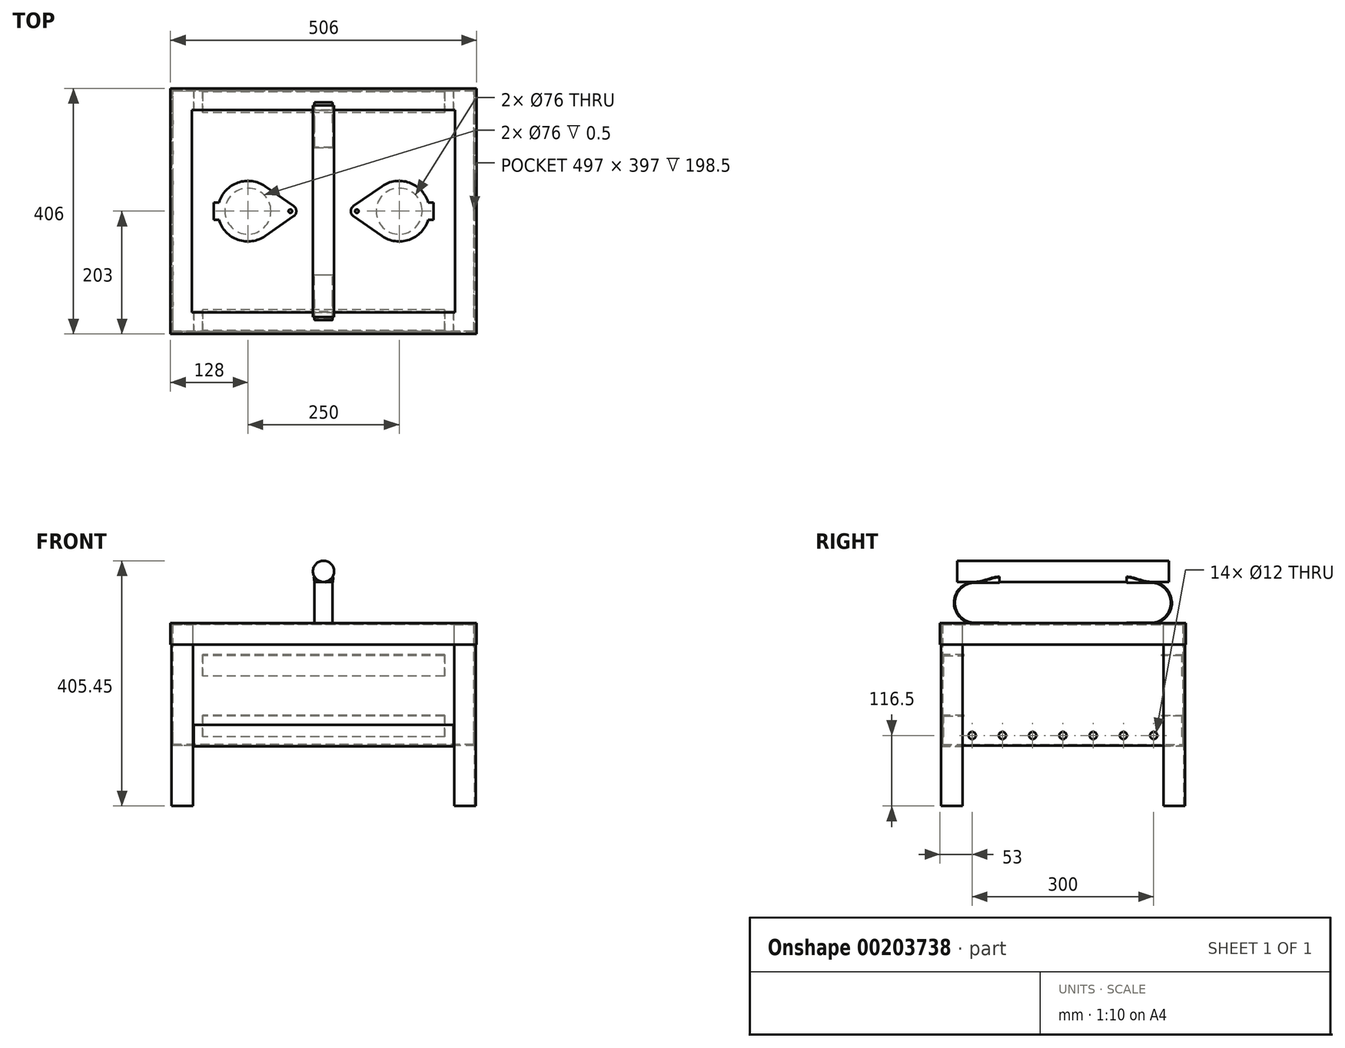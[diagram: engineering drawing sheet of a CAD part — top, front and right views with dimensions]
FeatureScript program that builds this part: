
annotation { "Feature Type Name" : "Feature", "Feature Type Description" : "" }
export const myFeature = defineFeature(function(context is Context, id is Id, definition is map)
    precondition{}
    {
        {
            var Q0;
            Q0=qCreatedBy(makeId("Top.planeOp"),FACE);
            var sketch = newSketch(context, id + "F0", { "sketchPlane" : qUnion([Q0])});
            skLineSegment(sketch, "E0.bottom", {"start": v(250, -200) * mm, "end": v(-250, -200) * mm});
            skLineSegment(sketch, "E0.top", {"start": v(250, 200) * mm, "end": v(-250, 200) * mm});
            skLineSegment(sketch, "E0.left", {"start": v(250, -200) * mm, "end": v(250, 200) * mm});
            skLineSegment(sketch, "E0.right", {"start": v(-250, -200) * mm, "end": v(-250, 200) * mm});
            skPoint(sketch, "E0.middle", {"position": v(0, 0) * mm});
            skSolve(sketch);
        }
        {
            var Q0;
            Q0 = qSketchRegion(id + "F0", true);
            extrude(context, id + "F1", {"entities" : qUnion([Q0]), "oppositeDirection" : true, "depth" : 200 * mm});
        }
        {
            var Q0;
            Q0=makeQuery(id+"F1.opExtrude","CAP_FACE",FACE,{"disambiguationData":[OSD([sQuery(id+"F0.wireOp",EDGE,"E0.bottom"),sQuery(id+"F0.wireOp",EDGE,"E0.top"),sQuery(id+"F0.wireOp",EDGE,"E0.left"),sQuery(id+"F0.wireOp",EDGE,"E0.right")])],"isStart":true});
            shell(context, id + "F2", {"entities" : qUnion([Q0]), "thickness" : 1.5 * mm});
        }
        {
            var Q0;
            Q0=qCreatedBy(makeId("Top.planeOp"),FACE);
            var sketch = newSketch(context, id + "F3", { "sketchPlane" : qUnion([Q0])});
            skLineSegment(sketch, "E1", {"start": v(-216, 201.5) * mm, "end": v(-251.5, 201.5) * mm});
            skLineSegment(sketch, "E2", {"start": v(-251.5, 201.5) * mm, "end": v(-251.5, 166) * mm});
            skLineSegment(sketch, "E3", {"start": v(-251.5, 166) * mm, "end": v(-250, 166) * mm});
            skLineSegment(sketch, "E4", {"start": v(-250, 166) * mm, "end": v(-250, 200) * mm});
            skLineSegment(sketch, "E5", {"start": v(-250, 200) * mm, "end": v(-216, 200) * mm});
            skLineSegment(sketch, "E6", {"start": v(-216, 200) * mm, "end": v(-216, 201.5) * mm});
            skSolve(sketch);
        }
        {
            var Q0;
            Q0 = qSketchRegion(id + "F3", true);
            var Q1;
            Q1=makeQuery(id+"F1.opExtrude","CAP_FACE",FACE,{"disambiguationData":[OSD([sQuery(id+"F0.wireOp",EDGE,"E0.bottom"),sQuery(id+"F0.wireOp",EDGE,"E0.top"),sQuery(id+"F0.wireOp",EDGE,"E0.left"),sQuery(id+"F0.wireOp",EDGE,"E0.right")])],"isStart":false});
            extrude(context, id + "F4", {"entities" : qUnion([Q0]), "oppositeDirection" : true, "endBoundEntityFace" : qUnion([Q1]), "depth" : 300 * mm});
        }
        {
            var Q0;
            Q0=makeQuery(id+"F4.opExtrude","SWEPT_BODY",BODY,{"disambiguationData":[OSD([sQuery(id+"F3.wireOp",EDGE,"E1"),sQuery(id+"F3.wireOp",EDGE,"E2"),sQuery(id+"F3.wireOp",EDGE,"E3"),sQuery(id+"F3.wireOp",EDGE,"E4"),sQuery(id+"F3.wireOp",EDGE,"E5"),sQuery(id+"F3.wireOp",EDGE,"E6")])]});
            var Q1;
            Q1=qCreatedBy(makeId("Front.planeOp"),FACE);
            mirror(context, id + "F5", {"entities" : qUnion([Q0]), "mirrorPlane" : qUnion([Q1])});
        }
        {
            var Q0;
            Q0=makeQuery(id+"F4.opExtrude","SWEPT_BODY",BODY,{"disambiguationData":[OSD([sQuery(id+"F3.wireOp",EDGE,"E1"),sQuery(id+"F3.wireOp",EDGE,"E2"),sQuery(id+"F3.wireOp",EDGE,"E3"),sQuery(id+"F3.wireOp",EDGE,"E4"),sQuery(id+"F3.wireOp",EDGE,"E5"),sQuery(id+"F3.wireOp",EDGE,"E6")])]});
            var Q1;
            Q1=makeQuery(id+"F5.opPattern","COPY",BODY,{"derivedFrom":makeQuery(id+"F4.opExtrude","SWEPT_BODY",BODY,{"disambiguationData":[OSD([sQuery(id+"F3.wireOp",EDGE,"E1"),sQuery(id+"F3.wireOp",EDGE,"E2"),sQuery(id+"F3.wireOp",EDGE,"E3"),sQuery(id+"F3.wireOp",EDGE,"E4"),sQuery(id+"F3.wireOp",EDGE,"E5"),sQuery(id+"F3.wireOp",EDGE,"E6")])]}),"instanceName":"1"});
            var Q2;
            Q2=qCreatedBy(makeId("Right.planeOp"),FACE);
            mirror(context, id + "F6", {"entities" : qUnion([Q0, Q1]), "mirrorPlane" : qUnion([Q2])});
        }
        {
            var Q0;
            Q0=qCreatedBy(makeId("Right.planeOp"),FACE);
            var sketch = newSketch(context, id + "F7", { "sketchPlane" : qUnion([Q0])});
            skLineSegment(sketch, "E7", {"start": v(163, -150) * mm, "end": v(198.5, -150) * mm});
            skLineSegment(sketch, "E8", {"start": v(198.5, -150) * mm, "end": v(198.5, -185.5) * mm});
            skLineSegment(sketch, "E9", {"start": v(198.5, -185.5) * mm, "end": v(197, -185.5) * mm});
            skLineSegment(sketch, "E10", {"start": v(197, -185.5) * mm, "end": v(197, -151.5) * mm});
            skLineSegment(sketch, "E11", {"start": v(197, -151.5) * mm, "end": v(163, -151.5) * mm});
            skLineSegment(sketch, "E12", {"start": v(163, -151.5) * mm, "end": v(163, -150) * mm});
            skSolve(sketch);
        }
        {
            var Q0;
            Q0 = qSketchRegion(id + "F7", true);
            extrude(context, id + "F8", {"entities" : qUnion([Q0]), "endBound" : BoundingType.SYMMETRIC, "depth" : 400 * mm});
        }
        {
            var Q0;
            Q0=makeQuery(id+"F8.opExtrude","SWEPT_BODY",BODY,{"disambiguationData":[OSD([sQuery(id+"F7.wireOp",EDGE,"E7"),sQuery(id+"F7.wireOp",EDGE,"E8"),sQuery(id+"F7.wireOp",EDGE,"E9"),sQuery(id+"F7.wireOp",EDGE,"E10"),sQuery(id+"F7.wireOp",EDGE,"E11"),sQuery(id+"F7.wireOp",EDGE,"E12")])]});
            var Q1;
            Q1=qCreatedBy(makeId("Front.planeOp"),FACE);
            mirror(context, id + "F9", {"entities" : qUnion([Q0]), "mirrorPlane" : qUnion([Q1])});
        }
        {
            var Q0;
            Q0=makeQuery(id+"F8.opExtrude","SWEPT_BODY",BODY,{"disambiguationData":[OSD([sQuery(id+"F7.wireOp",EDGE,"E7"),sQuery(id+"F7.wireOp",EDGE,"E8"),sQuery(id+"F7.wireOp",EDGE,"E9"),sQuery(id+"F7.wireOp",EDGE,"E10"),sQuery(id+"F7.wireOp",EDGE,"E11"),sQuery(id+"F7.wireOp",EDGE,"E12")])]});
            var Q1;
            Q1=makeQuery(id+"F9.opPattern","COPY",BODY,{"derivedFrom":makeQuery(id+"F8.opExtrude","SWEPT_BODY",BODY,{"disambiguationData":[OSD([sQuery(id+"F7.wireOp",EDGE,"E7"),sQuery(id+"F7.wireOp",EDGE,"E8"),sQuery(id+"F7.wireOp",EDGE,"E9"),sQuery(id+"F7.wireOp",EDGE,"E10"),sQuery(id+"F7.wireOp",EDGE,"E11"),sQuery(id+"F7.wireOp",EDGE,"E12")])]}),"instanceName":"1"});
            var Q2;
            Q2=makeQuery(id+"F1.opExtrude","SWEPT_EDGE",EDGE,{"disambiguationData":[OSD([sQuery(id+"F0.wireOp",EDGE,"E0.top"),sQuery(id+"F0.wireOp",EDGE,"E0.right")])]});
            transform(context, id + "F10", {"entities" : qUnion([Q0, Q1]), "transformType" : TransformType.TRANSLATION_DISTANCE, "transformDirection" : qUnion([Q2]), "distance" : 100 * mm, "makeCopy" : true});
        }
        {
            var Q0;
            Q0=makeQuery(id+"F1.opExtrude","SWEPT_FACE",FACE,{"disambiguationData":[OSD([sQuery(id+"F0.wireOp",EDGE,"E0.right")])]});
            var sketch = newSketch(context, id + "F11", { "sketchPlane" : qUnion([Q0])});
            skLineSegment(sketch, "E13", {"start": v(-221.22, -183.5) * mm, "end": v(207.24, -183.5) * mm, "construction": true});
            skCircle(sketch, "E14", {"center": v(0, -183.5) * mm, "radius": 6 * mm});
            skPoint(sketch, "E14.centerSnap0", {"position": v(-7, -183.5) * mm});
            skCircle(sketch, "E15.1.0.0", {"center": v(50, -183.5) * mm, "radius": 6 * mm});
            skCircle(sketch, "E15.2.0.0", {"center": v(100, -183.5) * mm, "radius": 6 * mm});
            skCircle(sketch, "E15.3.0.0", {"center": v(150, -183.5) * mm, "radius": 6 * mm});
            skLineSegment(sketch, "E15.direction1", {"start": v(0, -183.5) * mm, "end": v(50, -183.5) * mm, "construction": true});
            skCircle(sketch, "E16.1.0.0", {"center": v(-50, -183.5) * mm, "radius": 6 * mm});
            skCircle(sketch, "E16.2.0.0", {"center": v(-100, -183.5) * mm, "radius": 6 * mm});
            skCircle(sketch, "E16.3.0.0", {"center": v(-150, -183.5) * mm, "radius": 6 * mm});
            skLineSegment(sketch, "E16.direction1", {"start": v(0, -183.5) * mm, "end": v(-50, -183.5) * mm, "construction": true});
            skSolve(sketch);
        }
        {
            var Q0;
            Q0 = qSketchRegion(id + "F11", true);
            extrude(context, id + "F12", {"entities" : qUnion([Q0]), "operationType" : NewBodyOperationType.REMOVE, "endBound" : BoundingType.THROUGH_ALL, "oppositeDirection" : true, "depth" : 25 * mm});
        }
        {
            var Q0;
            Q0=qCreatedBy(makeId("Top.planeOp"),FACE);
            var sketch = newSketch(context, id + "F13", { "sketchPlane" : qUnion([Q0])});
            skLineSegment(sketch, "E17.bottom", {"start": v(-250, 200) * mm, "end": v(250, 200) * mm});
            skLineSegment(sketch, "E17.top", {"start": v(-250, -200) * mm, "end": v(250, -200) * mm});
            skLineSegment(sketch, "E17.left", {"start": v(-250, 200) * mm, "end": v(-250, -200) * mm});
            skLineSegment(sketch, "E17.right", {"start": v(250, 200) * mm, "end": v(250, -200) * mm});
            skSolve(sketch);
        }
        {
            var Q0;
            Q0 = qSketchRegion(id + "F13", true);
            extrude(context, id + "F14", {"entities" : qUnion([Q0]), "depth" : 1.5 * mm});
        }
        {
            var Q0;
            Q0=makeQuery(id+"F14.opExtrude","CAP_FACE",FACE,{"disambiguationData":[OSD([sQuery(id+"F13.wireOp",EDGE,"E17.bottom"),sQuery(id+"F13.wireOp",EDGE,"E17.top"),sQuery(id+"F13.wireOp",EDGE,"E17.left"),sQuery(id+"F13.wireOp",EDGE,"E17.right")])],"isStart":false});
            cPlane(context, id + "F15", {"entities" : qUnion([Q0]), "cplaneType" : CPlaneType.OFFSET, "offset" : 1 * mm, "width" : 150 * mm, "height" : 150 * mm});
        }
        {
            var Q0;
            Q0=qCreatedBy(id+"F15.planeOp",FACE);
            var sketch = newSketch(context, id + "F16", { "sketchPlane" : qUnion([Q0])});
            skLineSegment(sketch, "E18.0", {"start": v(-251.5, 201.5) * mm, "end": v(-251.5, 166) * mm, "construction": true});
            skLineSegment(sketch, "E19.0", {"start": v(-216, 201.5) * mm, "end": v(-251.5, 201.5) * mm, "construction": true});
            skLineSegment(sketch, "E20.bottom", {"start": v(-253, 203) * mm, "end": v(253, 203) * mm});
            skLineSegment(sketch, "E20.top", {"start": v(-253, -203) * mm, "end": v(253, -203) * mm});
            skLineSegment(sketch, "E20.left", {"start": v(-253, 203) * mm, "end": v(-253, -203) * mm});
            skLineSegment(sketch, "E20.right", {"start": v(253, 203) * mm, "end": v(253, -203) * mm});
            skLineSegment(sketch, "E21.0", {"start": v(216, -201.5) * mm, "end": v(251.5, -201.5) * mm, "construction": true});
            skLineSegment(sketch, "E22.0", {"start": v(251.5, -201.5) * mm, "end": v(251.5, -166) * mm, "construction": true});
            skSolve(sketch);
        }
        {
            var Q0;
            Q0 = qSketchRegion(id + "F16", true);
            extrude(context, id + "F17", {"entities" : qUnion([Q0]), "oppositeDirection" : true, "depth" : 35.5 * mm});
        }
        {
            var Q0;
            Q0=makeQuery(id+"F17.opExtrude","CAP_FACE",FACE,{"disambiguationData":[OSD([sQuery(id+"F16.wireOp",EDGE,"E20.bottom"),sQuery(id+"F16.wireOp",EDGE,"E20.top"),sQuery(id+"F16.wireOp",EDGE,"E20.left"),sQuery(id+"F16.wireOp",EDGE,"E20.right")])],"isStart":false});
            shell(context, id + "F18", {"entities" : qUnion([Q0]), "thickness" : 1.5 * mm});
        }
        {
            var Q0;
            Q0=makeQuery(id+"F17.opExtrude","CAP_FACE",FACE,{"disambiguationData":[OSD([sQuery(id+"F16.wireOp",EDGE,"E20.bottom"),sQuery(id+"F16.wireOp",EDGE,"E20.top"),sQuery(id+"F16.wireOp",EDGE,"E20.left"),sQuery(id+"F16.wireOp",EDGE,"E20.right")])],"isStart":true});
            var sketch = newSketch(context, id + "F19", { "sketchPlane" : qUnion([Q0])});
            skLineSegment(sketch, "E23.bottom", {"start": v(-217.5, 167.5) * mm, "end": v(217.5, 167.5) * mm});
            skLineSegment(sketch, "E23.top", {"start": v(-217.5, -167.5) * mm, "end": v(217.5, -167.5) * mm});
            skLineSegment(sketch, "E23.left", {"start": v(-217.5, 167.5) * mm, "end": v(-217.5, -167.5) * mm});
            skLineSegment(sketch, "E23.right", {"start": v(217.5, 167.5) * mm, "end": v(217.5, -167.5) * mm});
            skSolve(sketch);
        }
        {
            var Q0;
            Q0 = qSketchRegion(id + "F19", true);
            extrude(context, id + "F20", {"entities" : qUnion([Q0]), "operationType" : NewBodyOperationType.REMOVE, "endBound" : BoundingType.UP_TO_NEXT, "oppositeDirection" : true, "depth" : 25 * mm});
        }
        {
            var Q0;
            Q0=makeQuery(id+"F14.opExtrude","CAP_FACE",FACE,{"disambiguationData":[OSD([sQuery(id+"F13.wireOp",EDGE,"E17.bottom"),sQuery(id+"F13.wireOp",EDGE,"E17.top"),sQuery(id+"F13.wireOp",EDGE,"E17.left"),sQuery(id+"F13.wireOp",EDGE,"E17.right")])],"isStart":false});
            var sketch = newSketch(context, id + "F21", { "sketchPlane" : qUnion([Q0])});
            skLineSegment(sketch, "E24", {"start": v(-340.59, 0) * mm, "end": v(391.54, 0) * mm, "construction": true});
            skPoint(sketch, "E24.startSnap0", {"position": v(-250, 0) * mm});
            skPoint(sketch, "E24.endSnap0", {"position": v(-250, 0) * mm});
            skLineSegment(sketch, "E25", {"start": v(0, 278) * mm, "end": v(0, -285.77) * mm, "construction": true});
            skCircle(sketch, "E26", {"center": v(-125, 0) * mm, "radius": 38 * mm});
            skCircle(sketch, "E27", {"center": v(125, 0) * mm, "radius": 38 * mm});
            skSolve(sketch);
        }
        {
            var Q0;
            Q0 = qSketchRegion(id + "F21", true);
            extrude(context, id + "F22", {"entities" : qUnion([Q0]), "operationType" : NewBodyOperationType.REMOVE, "endBound" : BoundingType.UP_TO_NEXT, "oppositeDirection" : true, "depth" : 25 * mm});
        }
        {
            var Q0;
            Q0=makeQuery(id+"F14.opExtrude","CAP_FACE",FACE,{"disambiguationData":[OSD([sQuery(id+"F13.wireOp",EDGE,"E17.bottom"),sQuery(id+"F13.wireOp",EDGE,"E17.top"),sQuery(id+"F13.wireOp",EDGE,"E17.left"),sQuery(id+"F13.wireOp",EDGE,"E17.right")])],"isStart":false});
            var sketch = newSketch(context, id + "F23", { "sketchPlane" : qUnion([Q0])});
            skArc(sketch, "E28", {"start": v(-172.89, -14.38) * mm, "mid": v(-141.46, -47.21) * mm, "end": v(-96.43, -41.03) * mm});
            skCircle(sketch, "E29", {"center": v(-55, 0) * mm, "radius": 3 * mm});
            skArc(sketch, "E30", {"start": v(-49.29, -8.2) * mm, "mid": v(-45, 0) * mm, "end": v(-49.29, 8.2) * mm});
            skLineSegment(sketch, "E31", {"start": v(-96.43, 41.03) * mm, "end": v(-49.29, 8.2) * mm});
            skLineSegment(sketch, "E32", {"start": v(-49.29, -8.2) * mm, "end": v(-96.43, -41.03) * mm});
            skLineSegment(sketch, "E33.bottom", {"start": v(-172.89, -14.38) * mm, "end": v(-181.51, -14.38) * mm});
            skLineSegment(sketch, "E33.top", {"start": v(-172.89, 14.38) * mm, "end": v(-181.51, 14.38) * mm});
            skLineSegment(sketch, "E33.right", {"start": v(-181.51, -14.38) * mm, "end": v(-181.51, 14.38) * mm});
            skPoint(sketch, "E33.middle", {"position": v(-177.2, 0) * mm});
            skArc(sketch, "E34.trimOffspring", {"start": v(-96.43, 41.03) * mm, "mid": v(-141.46, 47.21) * mm, "end": v(-172.89, 14.38) * mm});
            skSolve(sketch);
        }
        {
            var Q0;
            Q0 = qSketchRegion(id + "F23", true);
            extrude(context, id + "F24", {"entities" : qUnion([Q0]), "depth" : 0.6 * mm});
        }
        {
            var Q0;
            Q0=makeQuery(id+"F24.opExtrude","SWEPT_BODY",BODY,{"disambiguationData":[OSD([sQuery(id+"F23.wireOp",EDGE,"E28"),sQuery(id+"F23.wireOp",EDGE,"E29"),sQuery(id+"F23.wireOp",EDGE,"E30"),sQuery(id+"F23.wireOp",EDGE,"E31"),sQuery(id+"F23.wireOp",EDGE,"E32"),sQuery(id+"F23.wireOp",EDGE,"E33.bottom"),sQuery(id+"F23.wireOp",EDGE,"E33.top"),sQuery(id+"F23.wireOp",EDGE,"E33.right"),sQuery(id+"F23.wireOp",EDGE,"E34.trimOffspring")])]});
            var Q1;
            Q1=qCreatedBy(makeId("Right.planeOp"),FACE);
            mirror(context, id + "F25", {"entities" : qUnion([Q0]), "mirrorPlane" : qUnion([Q1])});
        }
        {
            var Q0;
            Q0=qCreatedBy(makeId("Front.planeOp"),FACE);
            var sketch = newSketch(context, id + "F26", { "sketchPlane" : qUnion([Q0])});
            skCircle(sketch, "E35", {"center": v(0, 87.95) * mm, "radius": 17.5 * mm});
            skSolve(sketch);
        }
        {
            var Q0;
            Q0 = qSketchRegion(id + "F26", true);
            extrude(context, id + "F27", {"entities" : qUnion([Q0]), "endBound" : BoundingType.SYMMETRIC, "depth" : 350 * mm});
        }
        {
            var Q0;
            Q0=qCreatedBy(makeId("Right.planeOp"),FACE);
            var sketch = newSketch(context, id + "F28", { "sketchPlane" : qUnion([Q0])});
            skLineSegment(sketch, "E36", {"start": v(201.5, -166) * mm, "end": v(201.5, -201.5) * mm});
            skLineSegment(sketch, "E37", {"start": v(201.5, -201.5) * mm, "end": v(166, -201.5) * mm});
            skLineSegment(sketch, "E38", {"start": v(166, -201.5) * mm, "end": v(166, -200) * mm});
            skLineSegment(sketch, "E39", {"start": v(166, -200) * mm, "end": v(200, -200) * mm});
            skLineSegment(sketch, "E40", {"start": v(200, -200) * mm, "end": v(200, -166) * mm});
            skLineSegment(sketch, "E41", {"start": v(200, -166) * mm, "end": v(201.5, -166) * mm});
            skLineSegment(sketch, "E42", {"start": v(0, 31.45) * mm, "end": v(0, -269.26) * mm, "construction": true});
            skLineSegment(sketch, "E43.MirrorCS", {"start": v(-200, -166) * mm, "end": v(-201.5, -166) * mm});
            skLineSegment(sketch, "E44.MirrorCS", {"start": v(-166, -201.5) * mm, "end": v(-166, -200) * mm});
            skLineSegment(sketch, "E45.MirrorCS", {"start": v(-201.5, -166) * mm, "end": v(-201.5, -201.5) * mm});
            skLineSegment(sketch, "E46.MirrorCS", {"start": v(-201.5, -201.5) * mm, "end": v(-166, -201.5) * mm});
            skLineSegment(sketch, "E47.MirrorCS", {"start": v(-166, -200) * mm, "end": v(-200, -200) * mm});
            skLineSegment(sketch, "E48.MirrorCS", {"start": v(-200, -200) * mm, "end": v(-200, -166) * mm});
            skSolve(sketch);
        }
        {
            var Q0;
            Q0 = qSketchRegion(id + "F28", true);
            extrude(context, id + "F29", {"entities" : qUnion([Q0]), "endBound" : BoundingType.SYMMETRIC, "depth" : (500 - 35.5 * 2) * mm});
        }
        {
            var Q0;
            Q0=qCreatedBy(makeId("Right.planeOp"),FACE);
            var sketch = newSketch(context, id + "F30", { "sketchPlane" : qUnion([Q0])});
            skArc(sketch, "E49", {"start": v(-145.52, 70.45) * mm, "mid": v(-180, 35.98) * mm, "end": v(-145.52, 1.5) * mm});
            skLineSegment(sketch, "E50", {"start": v(-145.52, 1.5) * mm, "end": v(-105.52, 1.5) * mm});
            skLineSegment(sketch, "E51", {"start": v(-145.52, 70.45) * mm, "end": v(-83.43, 70.45) * mm, "construction": true});
            skLineSegment(sketch, "E52", {"start": v(175, 70.45) * mm, "end": v(-175, 70.45) * mm, "construction": true});
            skLineSegment(sketch, "E53.0", {"start": v(200, 1.5) * mm, "end": v(-200, 1.5) * mm, "construction": true});
            skLineSegment(sketch, "E54", {"start": v(-200, 1.5) * mm, "end": v(-200, 145.18) * mm, "construction": true});
            skLineSegment(sketch, "E55", {"start": v(-180, 1.5) * mm, "end": v(-180, 157.28) * mm, "construction": true});
            skLineSegment(sketch, "E56.0", {"start": v(-145.52, 3) * mm, "end": v(-105.52, 3) * mm});
            skArc(sketch, "E56.1", {"start": v(-145.52, 68.95) * mm, "mid": v(-178.5, 35.98) * mm, "end": v(-145.52, 3) * mm});
            skLineSegment(sketch, "E57", {"start": v(-105.52, 1.5) * mm, "end": v(-105.52, 3) * mm});
            skLineSegment(sketch, "E58", {"start": v(-145.52, 68.95) * mm, "end": v(-145.52, 70.45) * mm});
            skSolve(sketch);
        }
        {
            var Q0;
            Q0 = qSketchRegion(id + "F30", true);
            extrude(context, id + "F31", {"entities" : qUnion([Q0]), "endBound" : BoundingType.SYMMETRIC, "depth" : 30 * mm});
        }
        {
            var Q0;
            Q0=qCreatedBy(makeId("Front.planeOp"),FACE);
            cPlane(context, id + "F32", {"entities" : qUnion([Q0]), "cplaneType" : CPlaneType.OFFSET, "offset" : 105 * mm, "width" : 150 * mm, "height" : 150 * mm});
        }
        {
            var Q0;
            Q0=qCreatedBy(id+"F32.planeOp",FACE);
            var sketch = newSketch(context, id + "F33", { "sketchPlane" : qUnion([Q0])});
            skCircle(sketch, "E59.0", {"center": v(0, 87.95) * mm, "radius": 17.5 * mm, "construction": true});
            skPoint(sketch, "E60.0", {"position": v(-15, 70.45) * mm});
            skPoint(sketch, "E61.0", {"position": v(15, 70.45) * mm});
            skLineSegment(sketch, "E62", {"start": v(-15, 70.45) * mm, "end": v(-15, 93.12) * mm, "construction": true});
            skLineSegment(sketch, "E63", {"start": v(-15, 93.12) * mm, "end": v(-14.27, 93.12) * mm, "construction": true});
            skLineSegment(sketch, "E64", {"start": v(15, 70.45) * mm, "end": v(15, 91.23) * mm, "construction": true});
            skArc(sketch, "E65", {"start": v(-15, 78.94) * mm, "mid": v(0, 70.45) * mm, "end": v(15, 78.94) * mm});
            skArc(sketch, "E66", {"start": v(-16.29, 78.17) * mm, "mid": v(0, 68.95) * mm, "end": v(16.29, 78.17) * mm});
            skLineSegment(sketch, "E67", {"start": v(0, 87.95) * mm, "end": v(-21.29, 75.16) * mm, "construction": true});
            skLineSegment(sketch, "E68", {"start": v(0, 87.95) * mm, "end": v(20.76, 75.48) * mm, "construction": true});
            skLineSegment(sketch, "E69", {"start": v(-16.29, 78.17) * mm, "end": v(-15, 78.94) * mm});
            skLineSegment(sketch, "E70", {"start": v(15, 78.94) * mm, "end": v(16.29, 78.17) * mm});
            skSolve(sketch);
        }
        {
            var Q0;
            Q0=makeQuery(id+"F31.opExtrude","SWEPT_FACE",FACE,{"disambiguationData":[OSD([sQuery(id+"F30.wireOp",EDGE,"E58")])]});
            var sketch = newSketch(context, id + "F34", { "sketchPlane" : qUnion([Q0])});
            skLineSegment(sketch, "E71.0.0", {"start": v(15, 68.95) * mm, "end": v(15, 70.45) * mm});
            skLineSegment(sketch, "E71.0.1", {"start": v(15, 70.45) * mm, "end": v(-15, 70.45) * mm});
            skLineSegment(sketch, "E71.0.2", {"start": v(-15, 70.45) * mm, "end": v(-15, 68.95) * mm});
            skLineSegment(sketch, "E71.0.3", {"start": v(-15, 68.95) * mm, "end": v(15, 68.95) * mm});
            skSolve(sketch);
        }
        {
            var Q1;
            Q1 = qSketchRegion(id + "F34", true);
            var Q2;
            Q2 = qSketchRegion(id + "F33", true);
            loft(context, id + "F35", {"operationType" : NewBodyOperationType.ADD, "startCondition" : LoftEndDerivativeType.NORMAL_TO_PROFILE, "startMagnitude" : 1, "endCondition" : LoftEndDerivativeType.NORMAL_TO_PROFILE, "endMagnitude" : 1, "sheetProfilesArray" : [{ "sheetProfileEntities" : qUnion([Q1]) }, { "sheetProfileEntities" : qUnion([Q2]) }]});
        }
        {
            var Q0;
            Q0=makeQuery(id+"F31.opExtrude","SWEPT_BODY",BODY,{"disambiguationData":[OSD([sQuery(id+"F30.wireOp",EDGE,"E49"),sQuery(id+"F30.wireOp",EDGE,"E50"),sQuery(id+"F30.wireOp",EDGE,"E56.0"),sQuery(id+"F30.wireOp",EDGE,"E56.1"),sQuery(id+"F30.wireOp",EDGE,"E57"),sQuery(id+"F30.wireOp",EDGE,"E58")])]});
            var Q1;
            Q1=qCreatedBy(makeId("Front.planeOp"),FACE);
            mirror(context, id + "F36", {"entities" : qUnion([Q0]), "mirrorPlane" : qUnion([Q1])});
        }
    });
